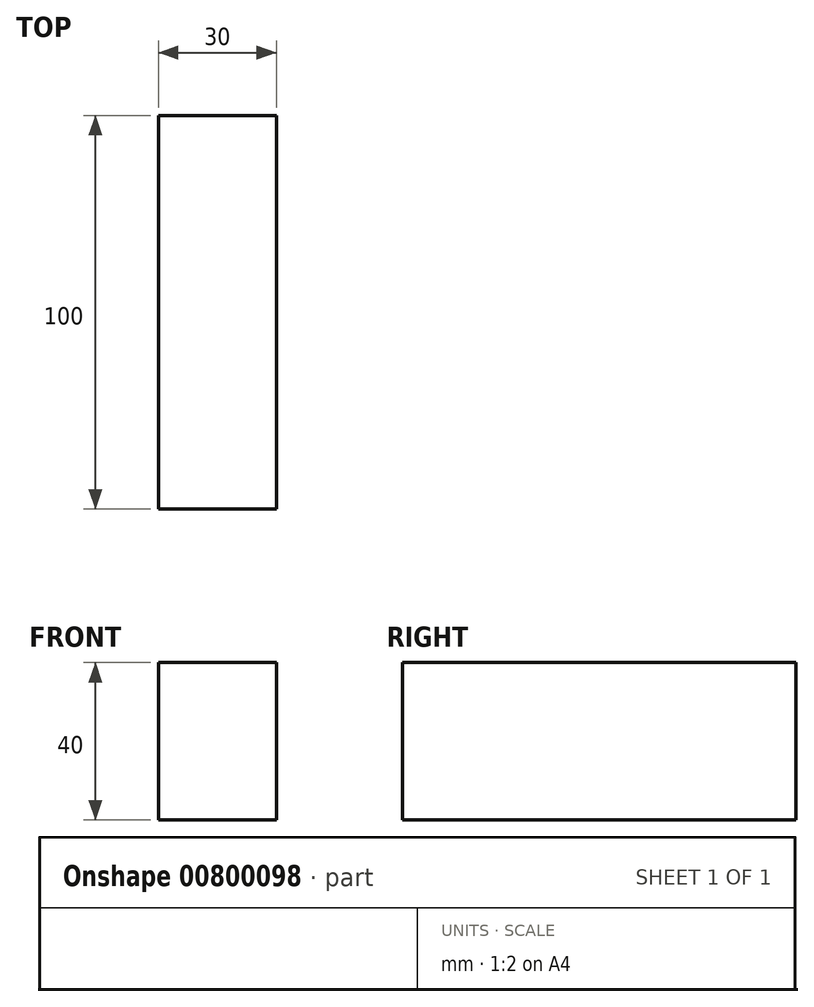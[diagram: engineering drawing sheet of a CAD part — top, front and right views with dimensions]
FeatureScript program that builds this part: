
annotation { "Feature Type Name" : "Feature", "Feature Type Description" : "" }
export const myFeature = defineFeature(function(context is Context, id is Id, definition is map)
    precondition{}
    {
        {
            var Q0;
            Q0=qCreatedBy(makeId("Front.planeOp"),FACE);
            var sketch = newSketch(context, id + "F0", { "sketchPlane" : qUnion([Q0])});
            skLineSegment(sketch, "E0.bottom", {"start": v(-15, 20) * mm, "end": v(15, 20) * mm});
            skLineSegment(sketch, "E0.top", {"start": v(-15, -20) * mm, "end": v(15, -20) * mm});
            skLineSegment(sketch, "E0.left", {"start": v(-15, 20) * mm, "end": v(-15, -20) * mm});
            skLineSegment(sketch, "E0.right", {"start": v(15, 20) * mm, "end": v(15, -20) * mm});
            skPoint(sketch, "E0.middle", {"position": v(0, 0) * mm});
            skSolve(sketch);
        }
        {
            var Q0;
            Q0=makeQuery(id+"F0.imprint","IMPRINT",FACE,{"disambiguationData":[TD([[makeQuery(id+"F0.imprint","IMPRINT",EDGE,{"derivedFrom":sQuery(id+"F0.wireOp",EDGE,"E0.bottom")}),-1.0]])]});
            extrude(context, id + "F1", {"entities" : qUnion([Q0]), "endBound" : BoundingType.SYMMETRIC, "depth" : 100 * mm, "offsetDistance" : 25 * mm});
        }
    });
